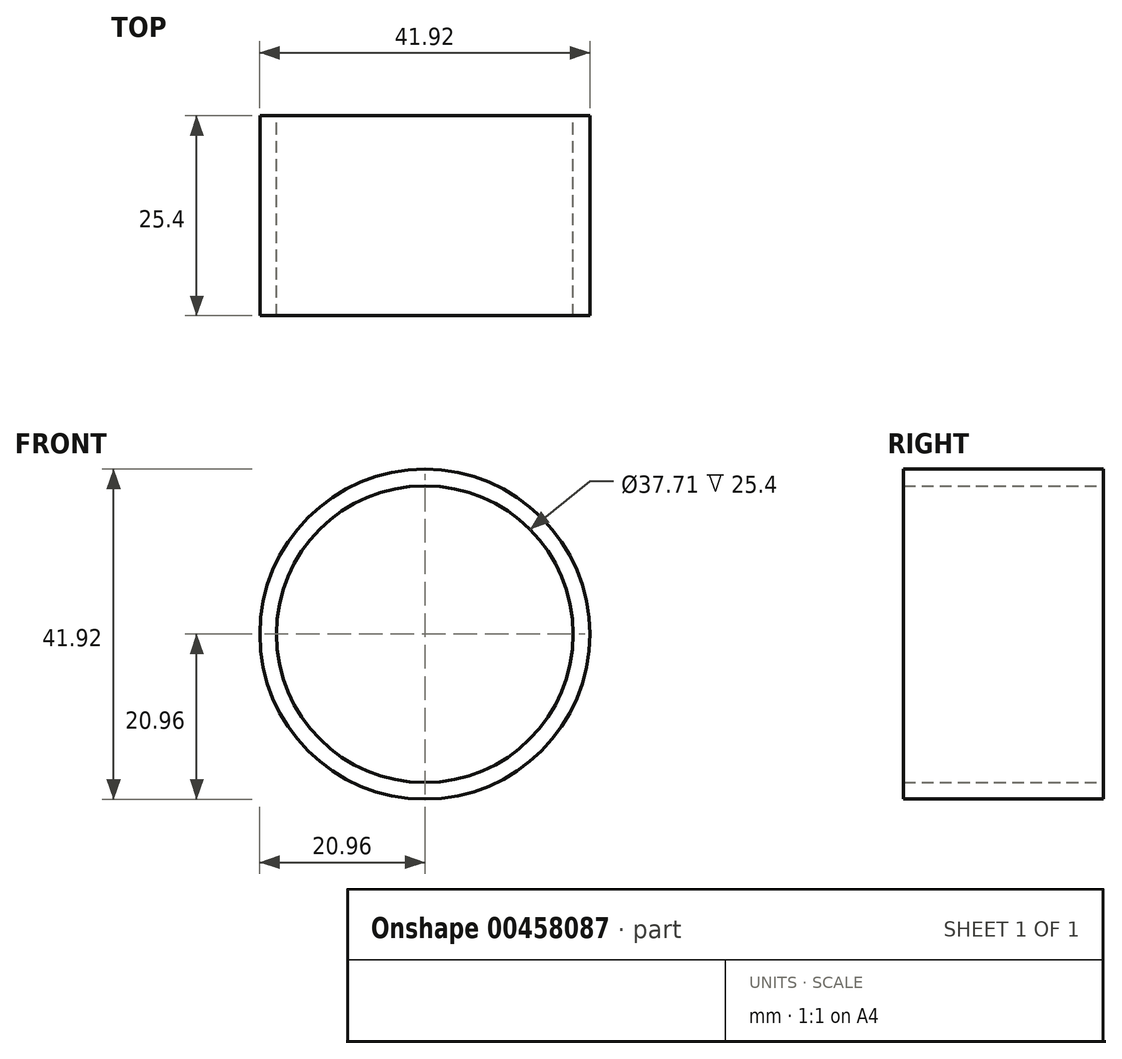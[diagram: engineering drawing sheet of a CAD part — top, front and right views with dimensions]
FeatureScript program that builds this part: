
annotation { "Feature Type Name" : "Feature", "Feature Type Description" : "" }
export const myFeature = defineFeature(function(context is Context, id is Id, definition is map)
    precondition{}
    {
        {
            var Q0;
            Q0=qCreatedBy(makeId("Front.planeOp"),FACE);
            var sketch = newSketch(context, id + "F0", { "sketchPlane" : qUnion([Q0])});
            skCircle(sketch, "E0", {"center": v(0, 0) * mm, "radius": 20.96 * mm});
            skCircle(sketch, "E1", {"center": v(0, 0) * mm, "radius": 18.86 * mm});
            skCircle(sketch, "E2", {"center": v(0, 0) * mm, "radius": 3.2 * mm});
            skSolve(sketch);
        }
        {
            var Q0;
            Q0=qCreatedBy(makeId("Front.planeOp"),FACE);
            var sketch = newSketch(context, id + "F1", { "sketchPlane" : qUnion([Q0])});
            skLineSegment(sketch, "E3", {"start": v(-2.22, 18.78) * mm, "end": v(-2.22, 16.68) * mm});
            skLineSegment(sketch, "E4", {"start": v(-2.22, 16.68) * mm, "end": v(1.48, 16.68) * mm});
            skLineSegment(sketch, "E5", {"start": v(1.48, 16.68) * mm, "end": v(1.48, 18.78) * mm});
            skPoint(sketch, "E6", {"position": v(0, 0) * mm});
            skSolve(sketch);
        }
        {
            var Q0;
            Q0=makeQuery(id+"F0.imprint","IMPRINT",FACE,{"disambiguationData":[TD([[makeQuery(id+"F0.imprint","IMPRINT",EDGE,{"derivedFrom":sQuery(id+"F0.wireOp",EDGE,"E0")}),1.0]])]});
            extrude(context, id + "F2", {"entities" : qUnion([Q0]), "depth" : 25.4 * mm});
        }
        {
            var Q0;
            Q0=sQuery(id+"Fc3X4Hr7MG3QDyN_0.1.F1.wireOp",EDGE,"E3");
            var Q1;
            Q1=sQuery(id+"Fc3X4Hr7MG3QDyN_0.1.F1.wireOp",EDGE,"E4");
            var Q2;
            Q2=sQuery(id+"Fc3X4Hr7MG3QDyN_0.1.F1.wireOp",EDGE,"E5");
            var Q3;
            Q3=sQuery(id+"F1.wireOp",EDGE,"E4");
            var Q4;
            Q4=sQuery(id+"F1.wireOp",EDGE,"E3");
            var Q5;
            Q5=sQuery(id+"F1.wireOp",EDGE,"E5");
            var Q6;
            Q6=sQuery(id+"Fc3X4Hr7MG3QDyN_0.14.F1.wireOp",EDGE,"E3");
            var Q7;
            Q7=sQuery(id+"Fc3X4Hr7MG3QDyN_0.14.F1.wireOp",EDGE,"E4");
            var Q8;
            Q8=sQuery(id+"Fc3X4Hr7MG3QDyN_0.14.F1.wireOp",EDGE,"E5");
            var Q9;
            Q9=sQuery(id+"Fc3X4Hr7MG3QDyN_0.13.F1.wireOp",EDGE,"E3");
            var Q10;
            Q10=sQuery(id+"Fc3X4Hr7MG3QDyN_0.13.F1.wireOp",EDGE,"E4");
            var Q11;
            Q11=sQuery(id+"Fc3X4Hr7MG3QDyN_0.13.F1.wireOp",EDGE,"E5");
            var Q12;
            Q12=sQuery(id+"Fc3X4Hr7MG3QDyN_0.12.F1.wireOp",EDGE,"E3");
            var Q13;
            Q13=sQuery(id+"Fc3X4Hr7MG3QDyN_0.12.F1.wireOp",EDGE,"E4");
            var Q14;
            Q14=sQuery(id+"Fc3X4Hr7MG3QDyN_0.12.F1.wireOp",EDGE,"E5");
            var Q15;
            Q15=sQuery(id+"Fc3X4Hr7MG3QDyN_0.11.F1.wireOp",EDGE,"E3");
            var Q16;
            Q16=sQuery(id+"Fc3X4Hr7MG3QDyN_0.11.F1.wireOp",EDGE,"E4");
            var Q17;
            Q17=sQuery(id+"Fc3X4Hr7MG3QDyN_0.11.F1.wireOp",EDGE,"E5");
            var Q18;
            Q18=sQuery(id+"Fc3X4Hr7MG3QDyN_0.2.F1.wireOp",EDGE,"E5");
            var Q19;
            Q19=sQuery(id+"Fc3X4Hr7MG3QDyN_0.2.F1.wireOp",EDGE,"E4");
            var Q20;
            Q20=sQuery(id+"Fc3X4Hr7MG3QDyN_0.2.F1.wireOp",EDGE,"E3");
            var Q21;
            Q21=sQuery(id+"Fc3X4Hr7MG3QDyN_0.3.F1.wireOp",EDGE,"E5");
            var Q22;
            Q22=sQuery(id+"Fc3X4Hr7MG3QDyN_0.3.F1.wireOp",EDGE,"E4");
            var Q23;
            Q23=sQuery(id+"Fc3X4Hr7MG3QDyN_0.3.F1.wireOp",EDGE,"E3");
            var Q24;
            Q24=sQuery(id+"Fc3X4Hr7MG3QDyN_0.4.F1.wireOp",EDGE,"E5");
            var Q25;
            Q25=sQuery(id+"Fc3X4Hr7MG3QDyN_0.4.F1.wireOp",EDGE,"E4");
            var Q26;
            Q26=sQuery(id+"Fc3X4Hr7MG3QDyN_0.4.F1.wireOp",EDGE,"E3");
            var Q27;
            Q27=sQuery(id+"Fc3X4Hr7MG3QDyN_0.5.F1.wireOp",EDGE,"E4");
            var Q28;
            Q28=sQuery(id+"Fc3X4Hr7MG3QDyN_0.5.F1.wireOp",EDGE,"E5");
            var Q29;
            Q29=sQuery(id+"Fc3X4Hr7MG3QDyN_0.6.F1.wireOp",EDGE,"E5");
            var Q30;
            Q30=sQuery(id+"Fc3X4Hr7MG3QDyN_0.5.F1.wireOp",EDGE,"E3");
            var Q31;
            Q31=sQuery(id+"Fc3X4Hr7MG3QDyN_0.6.F1.wireOp",EDGE,"E4");
            var Q32;
            Q32=sQuery(id+"Fc3X4Hr7MG3QDyN_0.6.F1.wireOp",EDGE,"E3");
            var Q33;
            Q33=sQuery(id+"Fc3X4Hr7MG3QDyN_0.7.F1.wireOp",EDGE,"E4");
            var Q34;
            Q34=sQuery(id+"Fc3X4Hr7MG3QDyN_0.7.F1.wireOp",EDGE,"E5");
            var Q35;
            Q35=sQuery(id+"Fc3X4Hr7MG3QDyN_0.7.F1.wireOp",EDGE,"E3");
            var Q36;
            Q36=sQuery(id+"Fc3X4Hr7MG3QDyN_0.8.F1.wireOp",EDGE,"E4");
            var Q37;
            Q37=sQuery(id+"Fc3X4Hr7MG3QDyN_0.8.F1.wireOp",EDGE,"E3");
            var Q38;
            Q38=sQuery(id+"Fc3X4Hr7MG3QDyN_0.8.F1.wireOp",EDGE,"E5");
            var Q39;
            Q39=sQuery(id+"Fc3X4Hr7MG3QDyN_0.9.F1.wireOp",EDGE,"E4");
            var Q40;
            Q40=sQuery(id+"Fc3X4Hr7MG3QDyN_0.9.F1.wireOp",EDGE,"E3");
            var Q41;
            Q41=sQuery(id+"Fc3X4Hr7MG3QDyN_0.9.F1.wireOp",EDGE,"E5");
            var Q42;
            Q42=sQuery(id+"Fc3X4Hr7MG3QDyN_0.10.F1.wireOp",EDGE,"E3");
            var Q43;
            Q43=sQuery(id+"Fc3X4Hr7MG3QDyN_0.10.F1.wireOp",EDGE,"E4");
            var Q44;
            Q44=sQuery(id+"Fc3X4Hr7MG3QDyN_0.10.F1.wireOp",EDGE,"E5");
            extrude(context, id + "F3", {"bodyType" : ToolBodyType.SURFACE, "surfaceEntities" : qUnion([Q0, Q1, Q2, Q3, Q4, Q5, Q6, Q7, Q8, Q9, Q10, Q11, Q12, Q13, Q14, Q15, Q16, Q17, Q18, Q19, Q20, Q21, Q22, Q23, Q24, Q25, Q26, Q27, Q28, Q29, Q30, Q31, Q32, Q33, Q34, Q35, Q36, Q37, Q38, Q39, Q40, Q41, Q42, Q43, Q44]), "depth" : 25.4 * mm});
        }
    });
